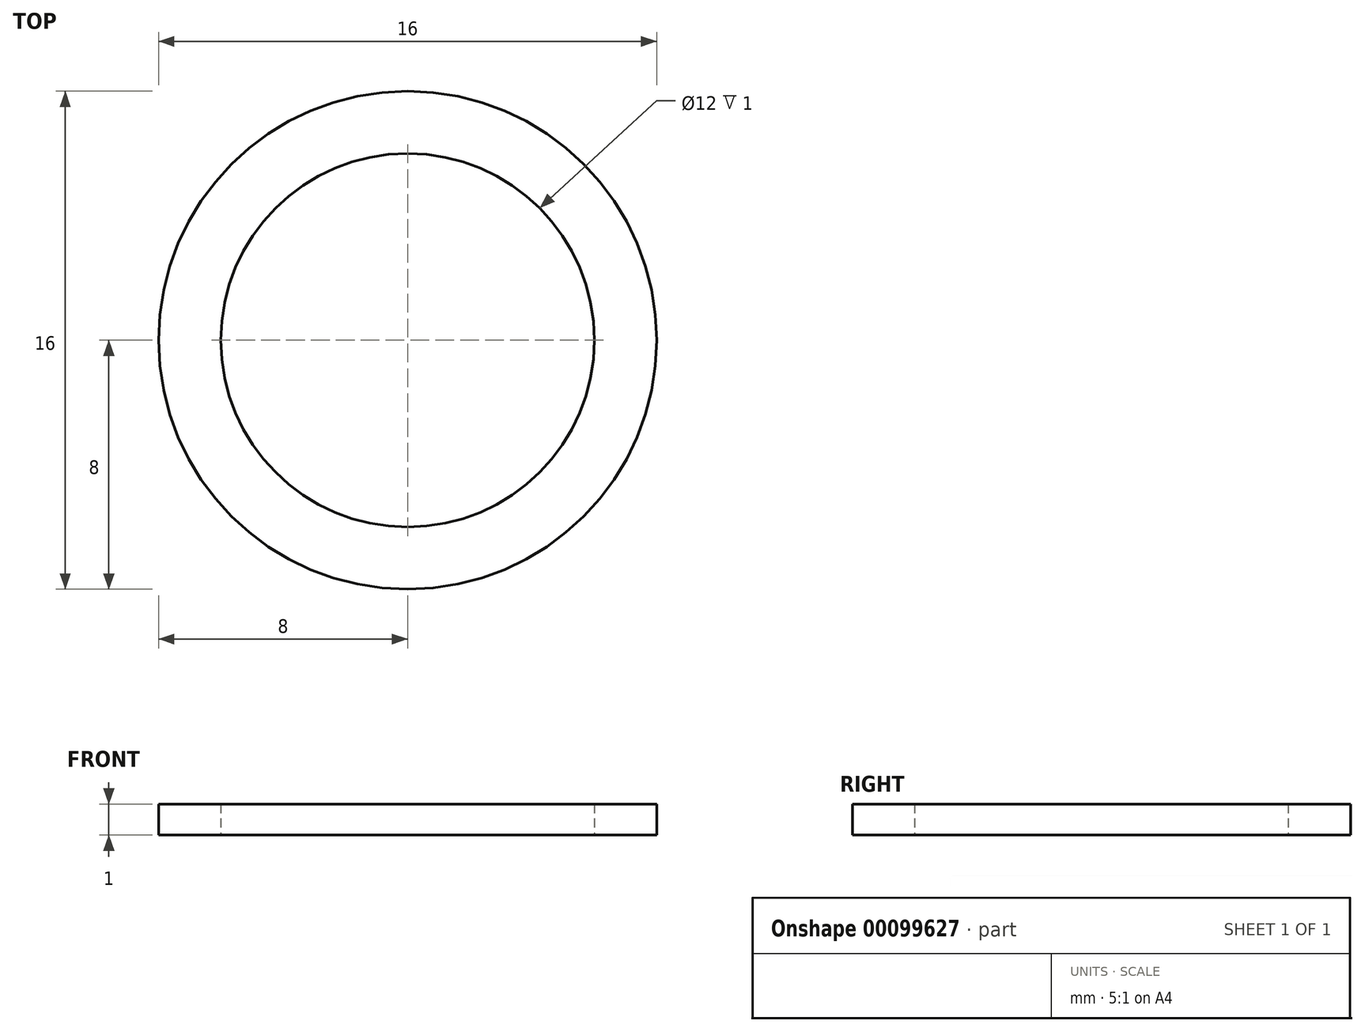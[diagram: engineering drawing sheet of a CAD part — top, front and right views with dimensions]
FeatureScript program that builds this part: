
annotation { "Feature Type Name" : "Feature", "Feature Type Description" : "" }
export const myFeature = defineFeature(function(context is Context, id is Id, definition is map)
    precondition{}
    {
        {
            var Q0;
            Q0=qCreatedBy(makeId("Top.planeOp"),FACE);
            var sketch = newSketch(context, id + "F0", { "sketchPlane" : qUnion([Q0])});
            skCircle(sketch, "E0", {"center": v(0, 0) * mm, "radius": 8 * mm});
            skCircle(sketch, "E1", {"center": v(0, 0) * mm, "radius": 6 * mm});
            skSolve(sketch);
        }
        {
            var Q0;
            Q0=makeQuery(id+"F0.imprint","IMPRINT",FACE,{"disambiguationData":[TD([[makeQuery(id+"F0.imprint","IMPRINT",EDGE,{"derivedFrom":sQuery(id+"F0.wireOp",EDGE,"E0")}),1.0]])]});
            extrude(context, id + "F1", {"entities" : qUnion([Q0]), "depth" : 1 * mm});
        }
    });
